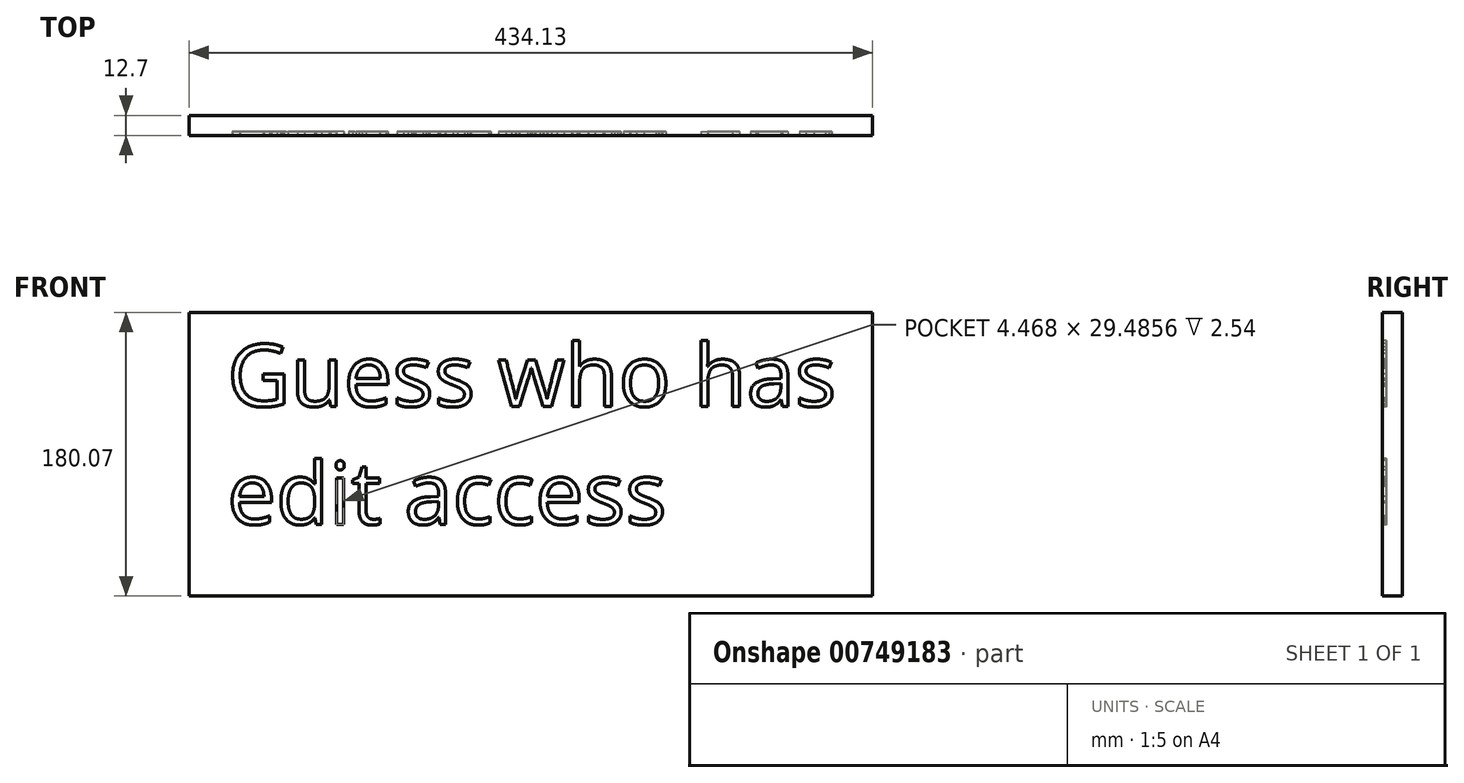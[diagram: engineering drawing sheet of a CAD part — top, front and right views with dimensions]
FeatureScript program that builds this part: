
annotation { "Feature Type Name" : "Feature", "Feature Type Description" : "" }
export const myFeature = defineFeature(function(context is Context, id is Id, definition is map)
    precondition{}
    {
        {
            var Q0;
            Q0=qCreatedBy(makeId("Front.planeOp"),FACE);
            var sketch = newSketch(context, id + "F0", { "sketchPlane" : qUnion([Q0])});
            skLineSegment(sketch, "E0.bottom", {"start": v(0, 0) * mm, "end": v(434.13, 0) * mm});
            skLineSegment(sketch, "E0.top", {"start": v(0, -180.07) * mm, "end": v(434.13, -180.07) * mm});
            skLineSegment(sketch, "E0.left", {"start": v(0, 0) * mm, "end": v(0, -180.07) * mm});
            skLineSegment(sketch, "E0.right", {"start": v(434.13, 0) * mm, "end": v(434.13, -180.07) * mm});
            skSolve(sketch);
        }
        {
            var Q0;
            Q0=makeQuery(id+"F0.imprint","IMPRINT",FACE,{"disambiguationData":[TD([[makeQuery(id+"F0.imprint","IMPRINT",EDGE,{"derivedFrom":sQuery(id+"F0.wireOp",EDGE,"E0.bottom")}),-1.0]])]});
            extrude(context, id + "F1", {"entities" : qUnion([Q0]), "depth" : 12.7 * mm});
        }
        {
            var Q0;
            Q0=makeQuery(id+"F1.opExtrude","CAP_FACE",FACE,{"disambiguationData":[OSD([sQuery(id+"F0.wireOp",EDGE,"E0.bottom"),sQuery(id+"F0.wireOp",EDGE,"E0.top"),sQuery(id+"F0.wireOp",EDGE,"E0.left"),sQuery(id+"F0.wireOp",EDGE,"E0.right")])],"isStart":false});
            var sketch = newSketch(context, id + "F2", { "sketchPlane" : qUnion([Q0])});
            skText(sketch, "E1", { "text": "Guess who has \nedit access", "fontName": "OpenSans-Regular.ttf"});
            const initialGuessF2  = {"E1": [0.0243, -0.05956, 1, 0, 0.03967]};
            skSetInitialGuess(sketch, initialGuessF2);
            skSolve(sketch);
        }
        {
            var Q0;
            Q0=qSketchRegion(id+"F2",true);
            extrude(context, id + "F3", {"entities" : qUnion([Q0]), "operationType" : NewBodyOperationType.REMOVE, "oppositeDirection" : true, "depth" : 2.54 * mm});
        }
    });
